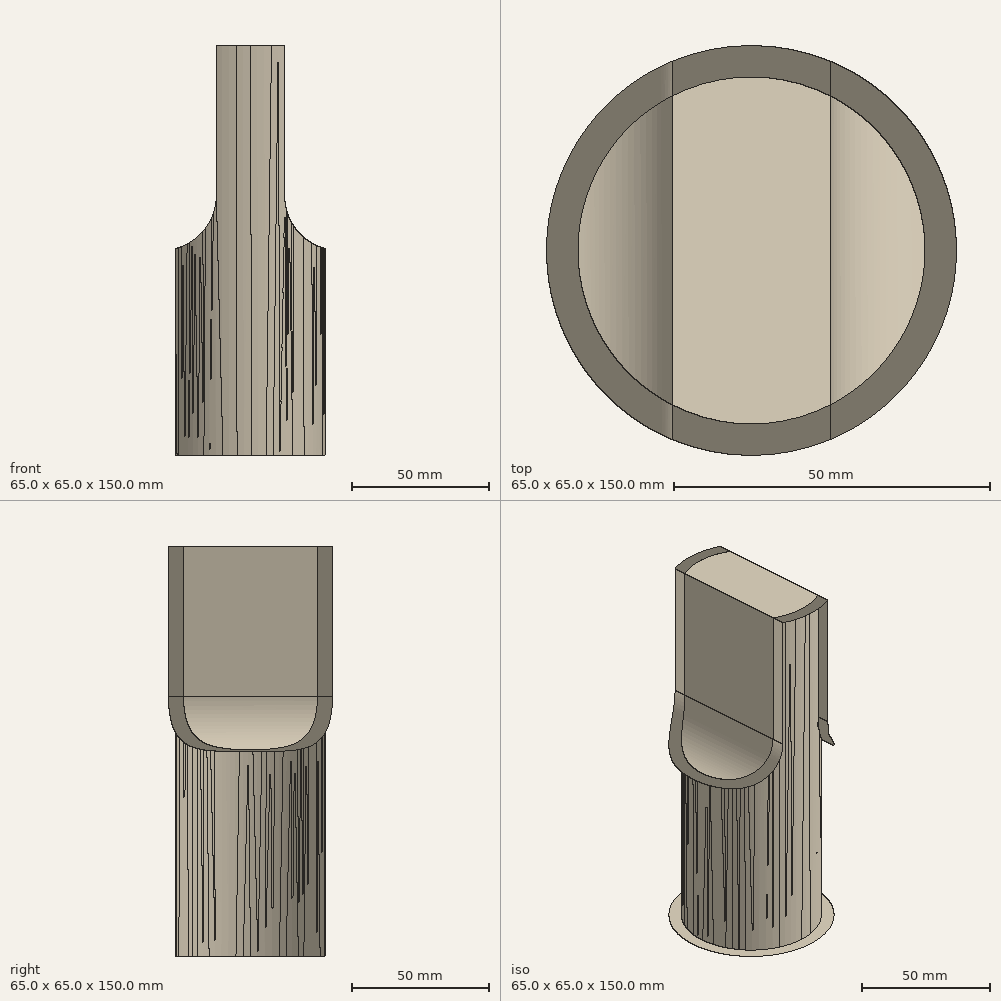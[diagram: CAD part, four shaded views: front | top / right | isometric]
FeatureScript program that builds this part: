
annotation { "Feature Type Name" : "Feature", "Feature Type Description" : "" }
export const myFeature = defineFeature(function(context is Context, id is Id, definition is map)
    precondition{}
    {
        {
            var Q0;
            Q0=qCreatedBy(makeId("Top.planeOp"),FACE);
            var sketch = newSketch(context, id + "F0", { "sketchPlane" : qUnion([Q0])});
            skCircle(sketch, "E0", {"center": v(0, 0) * mm, "radius": 27.5 * mm});
            skCircle(sketch, "E1", {"center": v(0, 0) * mm, "radius": 32.5 * mm});
            skSolve(sketch);
        }
        {
            var Q0;
            Q0=makeQuery(id+"F0.imprint","IMPRINT",FACE,{"disambiguationData":[TD([[makeQuery(id+"F0.imprint","IMPRINT",EDGE,{"derivedFrom":sQuery(id+"F0.wireOp",EDGE,"E0")}),1.0]])]});
            extrude(context, id + "F1", {"entities" : qUnion([Q0]), "depth" : 150 * mm, "offsetDistance" : 25 * mm});
        }
        {
            var Q0;
            Q0=qSketchRegion(id+"F0",true);
            extrude(context, id + "F2", {"entities" : qUnion([Q0]), "depth" : 150 * mm, "offsetDistance" : 25 * mm});
        }
        {
            var Q0;
            Q0=qCreatedBy(makeId("Front.planeOp"),FACE);
            var sketch = newSketch(context, id + "F3", { "sketchPlane" : qUnion([Q0])});
            skLineSegment(sketch, "E2.bottom", {"start": v(55.46, 165) * mm, "end": v(12.5, 165) * mm});
            skLineSegment(sketch, "E2.top", {"start": v(55.46, 75) * mm, "end": v(32.5, 75) * mm});
            skLineSegment(sketch, "E2.left", {"start": v(55.46, 165) * mm, "end": v(55.46, 75) * mm});
            skLineSegment(sketch, "E2.right", {"start": v(12.5, 165) * mm, "end": v(12.5, 95) * mm});
            skPoint(sketch, "E3.visualSharp", {"position": v(12.5, 75) * mm});
            skArc(sketch, "E3.filletArc", {"start": v(12.5, 95) * mm, "mid": v(18.36, 80.86) * mm, "end": v(32.5, 75) * mm});
            skLineSegment(sketch, "E4", {"start": v(0, 0) * mm, "end": v(0, 119.84) * mm, "construction": true});
            skPoint(sketch, "E5.MirrorP", {"position": v(-12.5, 75) * mm});
            skLineSegment(sketch, "E6.MirrorCS", {"start": v(-55.46, 165) * mm, "end": v(-12.5, 165) * mm});
            skLineSegment(sketch, "E7.MirrorCS", {"start": v(-55.46, 165) * mm, "end": v(-55.46, 75) * mm});
            skLineSegment(sketch, "E8.MirrorCS", {"start": v(-55.46, 75) * mm, "end": v(-32.5, 75) * mm});
            skLineSegment(sketch, "E9.MirrorCS", {"start": v(-12.5, 165) * mm, "end": v(-12.5, 95) * mm});
            skArc(sketch, "E10.MirrorCS", {"start": v(-12.5, 95) * mm, "mid": v(-18.36, 80.86) * mm, "end": v(-32.5, 75) * mm});
            skSolve(sketch);
        }
        {
            var Q0;
            Q0=qSketchRegion(id+"F3",true);
            extrude(context, id + "F4", {"entities" : qUnion([Q0]), "operationType" : NewBodyOperationType.REMOVE, "oppositeDirection" : true, "depth" : 100 * mm, "symmetric" : true});
        }
    });
